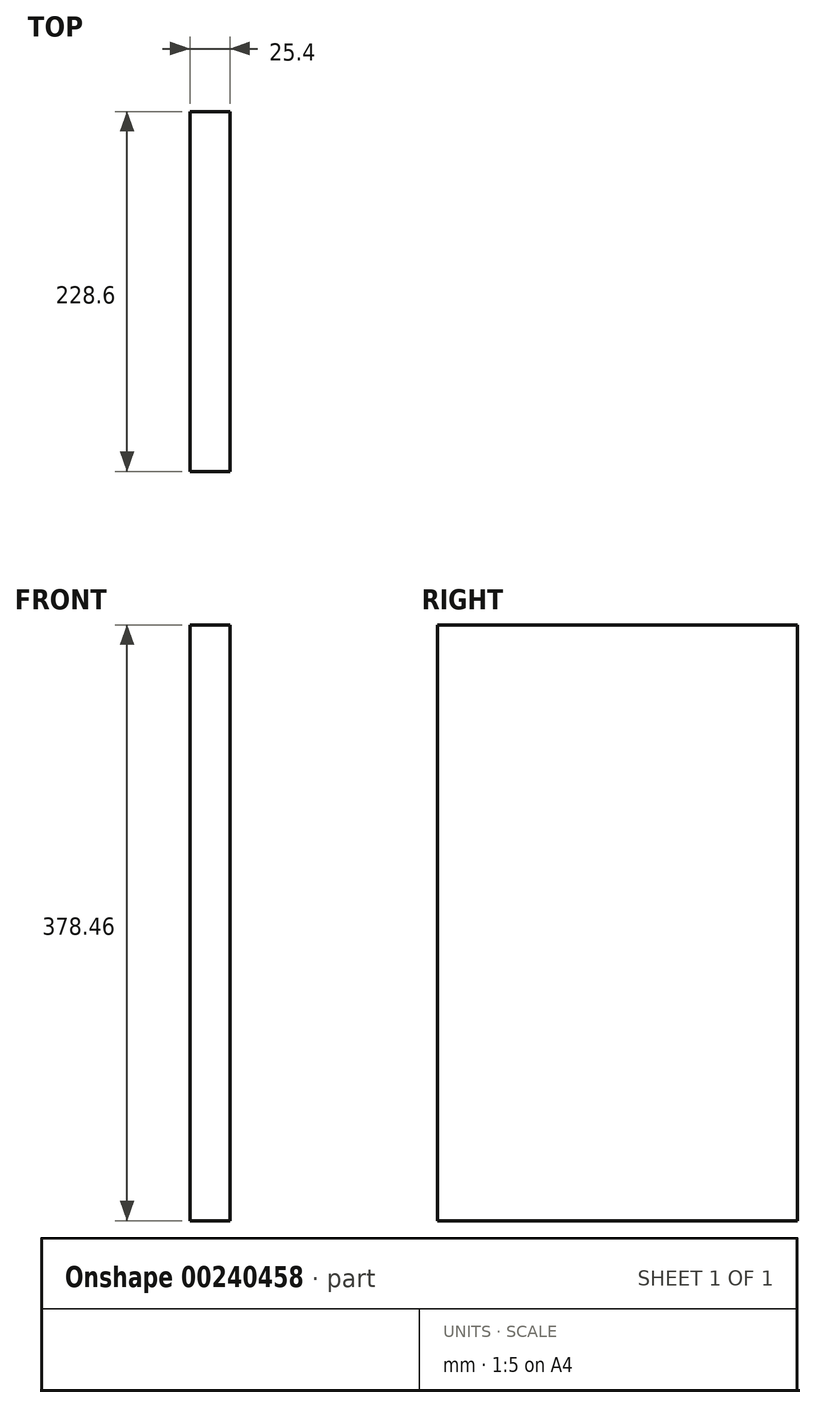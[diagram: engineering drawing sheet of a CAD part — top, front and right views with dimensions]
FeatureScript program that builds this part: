
annotation { "Feature Type Name" : "Feature", "Feature Type Description" : "" }
export const myFeature = defineFeature(function(context is Context, id is Id, definition is map)
    precondition{}
    {
        {
            var Q0;
            Q0=qCreatedBy(makeId("Right.planeOp"),FACE);
            var sketch = newSketch(context, id + "F0", { "sketchPlane" : qUnion([Q0])});
            skLineSegment(sketch, "E0.bottom", {"start": v(-114.3, -189.23) * mm, "end": v(114.3, -189.23) * mm});
            skLineSegment(sketch, "E0.top", {"start": v(-114.3, 189.23) * mm, "end": v(114.3, 189.23) * mm});
            skLineSegment(sketch, "E0.left", {"start": v(-114.3, -189.23) * mm, "end": v(-114.3, 189.23) * mm});
            skLineSegment(sketch, "E0.right", {"start": v(114.3, -189.23) * mm, "end": v(114.3, 189.23) * mm});
            skPoint(sketch, "E0.middle", {"position": v(0, 0) * mm});
            skSolve(sketch);
        }
        {
            var Q0;
            Q0=makeQuery(id+"F0.imprint","IMPRINT",FACE,{"disambiguationData":[TD([[makeQuery(id+"F0.imprint","IMPRINT",EDGE,{"derivedFrom":sQuery(id+"F0.wireOp",EDGE,"E0.bottom")}),1.0]])]});
            extrude(context, id + "F1", {"entities" : qUnion([Q0]), "depth" : 25.4 * mm});
        }
    });
